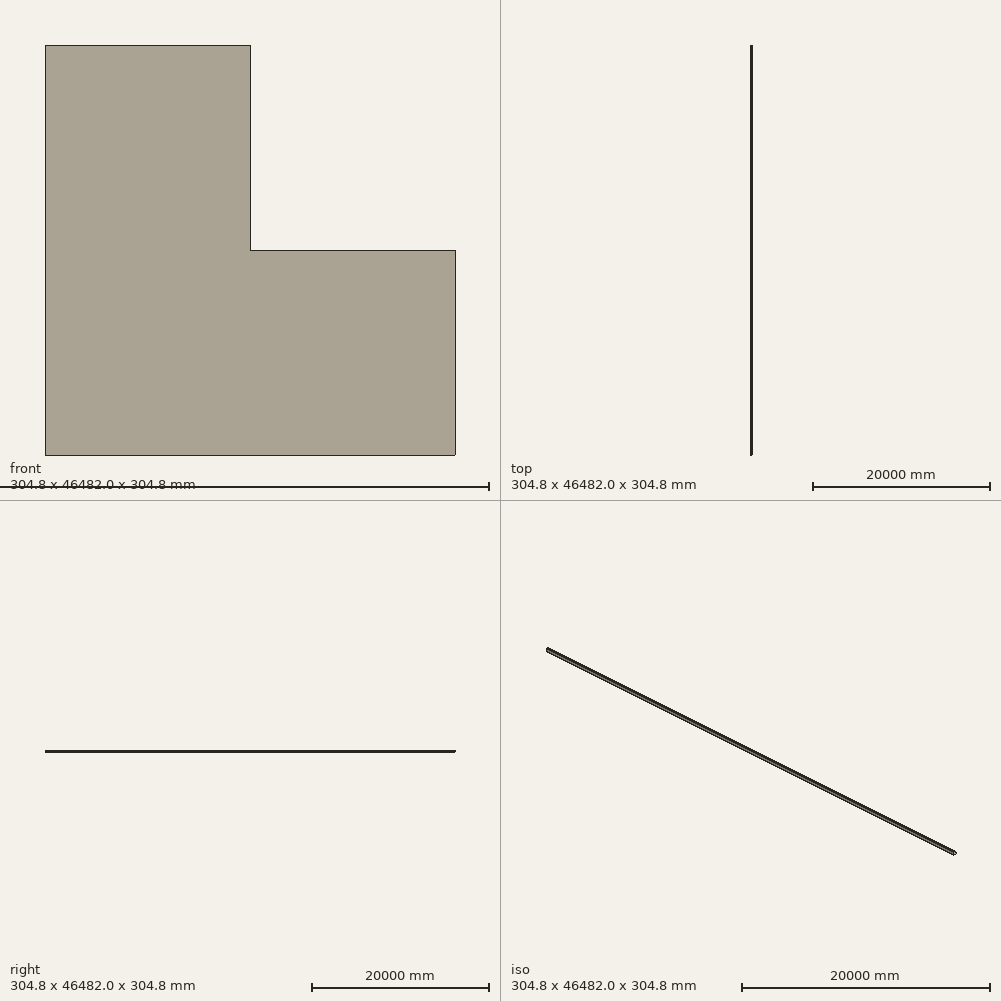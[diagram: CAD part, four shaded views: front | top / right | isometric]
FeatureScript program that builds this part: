
annotation { "Feature Type Name" : "Feature", "Feature Type Description" : "" }
export const myFeature = defineFeature(function(context is Context, id is Id, definition is map)
    precondition{}
    {
        {
            var Q0;
            Q0=qCreatedBy(makeId("Front.planeOp"),FACE);
            var sketch = newSketch(context, id + "F0", { "sketchPlane" : qUnion([Q0])});
            skLineSegment(sketch, "E0", {"start": v(0, 0) * mm, "end": v(0, 304.8) * mm});
            skLineSegment(sketch, "E1", {"start": v(0, 304.8) * mm, "end": v(152.4, 304.8) * mm});
            skLineSegment(sketch, "E2", {"start": v(152.4, 304.8) * mm, "end": v(152.4, 152.4) * mm});
            skLineSegment(sketch, "E3", {"start": v(152.4, 152.4) * mm, "end": v(304.8, 152.4) * mm});
            skLineSegment(sketch, "E4", {"start": v(304.8, 152.4) * mm, "end": v(304.8, 0) * mm});
            skLineSegment(sketch, "E5", {"start": v(304.8, 0) * mm, "end": v(0, 0) * mm});
            skSolve(sketch);
        }
        {
            var Q0;
            Q0 = qSketchRegion(id + "F0", true);
            extrude(context, id + "F1", {"entities" : qUnion([Q0]), "depth" : 46482 * mm, "offsetDistance" : 25.4 * mm});
        }
    });
